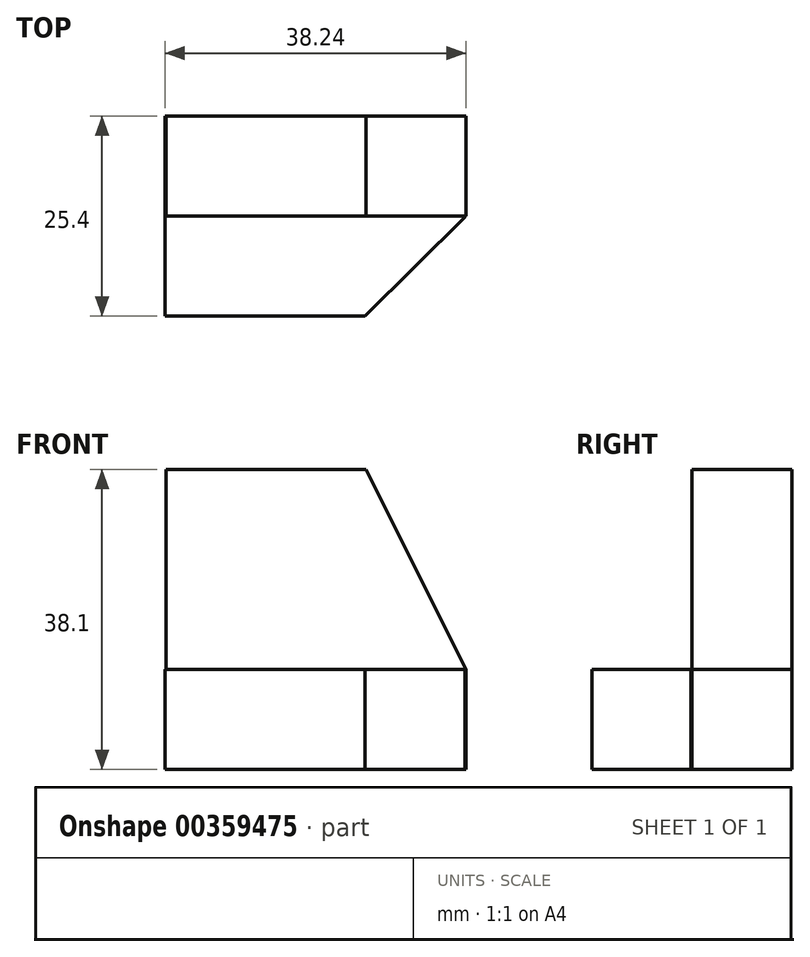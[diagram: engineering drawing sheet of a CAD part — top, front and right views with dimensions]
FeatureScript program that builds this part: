
annotation { "Feature Type Name" : "Feature", "Feature Type Description" : "" }
export const myFeature = defineFeature(function(context is Context, id is Id, definition is map)
    precondition{}
    {
        {
            var Q0;
            Q0=qCreatedBy(makeId("Front.planeOp"),FACE);
            var sketch = newSketch(context, id + "F0", { "sketchPlane" : qUnion([Q0])});
            skLineSegment(sketch, "E0", {"start": v(17, 44.03) * mm, "end": v(17, 5.93) * mm});
            skLineSegment(sketch, "E1", {"start": v(17, 5.93) * mm, "end": v(55.1, 5.93) * mm});
            skLineSegment(sketch, "E2", {"start": v(55.1, 5.93) * mm, "end": v(55.1, 44.03) * mm});
            skLineSegment(sketch, "E3", {"start": v(55.1, 44.03) * mm, "end": v(17, 44.03) * mm});
            skSolve(sketch);
        }
        {
            var Q0;
            Q0=makeQuery(id+"F0.imprint","IMPRINT",FACE,{"disambiguationData":[TD([[makeQuery(id+"F0.imprint","IMPRINT",EDGE,{"derivedFrom":sQuery(id+"F0.wireOp",EDGE,"E0")}),1.0]])]});
            extrude(context, id + "F1", {"entities" : qUnion([Q0]), "depth" : 12.7 * mm});
        }
        {
            var Q0;
            Q0=qCreatedBy(makeId("Front.planeOp"),FACE);
            var sketch = newSketch(context, id + "F2", { "sketchPlane" : qUnion([Q0])});
            skLineSegment(sketch, "E4", {"start": v(16.86, 18.63) * mm, "end": v(54.96, 18.63) * mm});
            skLineSegment(sketch, "E5", {"start": v(54.96, 18.63) * mm, "end": v(54.96, 5.93) * mm});
            skLineSegment(sketch, "E6", {"start": v(54.96, 5.93) * mm, "end": v(16.86, 5.93) * mm});
            skLineSegment(sketch, "E7", {"start": v(16.86, 5.93) * mm, "end": v(16.86, 18.63) * mm});
            skSolve(sketch);
        }
        {
            var Q0;
            Q0 = qSketchRegion(id + "F2", true);
            extrude(context, id + "F3", {"entities" : qUnion([Q0]), "operationType" : NewBodyOperationType.ADD, "depth" : 25.4 * mm});
        }
        {
            var Q0;
            Q0=qCreatedBy(makeId("Top.planeOp"),FACE);
            var sketch = newSketch(context, id + "F4", { "sketchPlane" : qUnion([Q0])});
            skLineSegment(sketch, "E8", {"start": v(55.1, -12.7) * mm, "end": v(42.26, -25.4) * mm});
            skLineSegment(sketch, "E9", {"start": v(42.26, -25.4) * mm, "end": v(54.96, -25.4) * mm});
            skLineSegment(sketch, "E10", {"start": v(54.96, -25.4) * mm, "end": v(55.1, -12.7) * mm});
            skSolve(sketch);
        }
        {
            var Q0;
            Q0 = qSketchRegion(id + "F4", true);
            extrude(context, id + "F5", {"entities" : qUnion([Q0]), "operationType" : NewBodyOperationType.REMOVE, "depth" : 25.4 * mm});
        }
        {
            var Q0;
            Q0=qCreatedBy(makeId("Front.planeOp"),FACE);
            var sketch = newSketch(context, id + "F6", { "sketchPlane" : qUnion([Q0])});
            skLineSegment(sketch, "E11", {"start": v(42.4, 44.03) * mm, "end": v(55.1, 18.63) * mm});
            skLineSegment(sketch, "E12", {"start": v(55.1, 18.63) * mm, "end": v(55.1, 44.03) * mm});
            skLineSegment(sketch, "E13", {"start": v(55.1, 44.03) * mm, "end": v(42.4, 44.03) * mm});
            skSolve(sketch);
        }
        {
            var Q0;
            Q0 = qSketchRegion(id + "F6", true);
            extrude(context, id + "F7", {"entities" : qUnion([Q0]), "operationType" : NewBodyOperationType.REMOVE, "depth" : 12.7 * mm});
        }
    });
